# Revit family: PC6080B
name_source: partatom
category: Luminarias
units: mm (PartAtom-declared; Revit-internal decimal feet)

## family parameters
Compartido = Sí
Corte con vacíos al cargar = No
Cota de conector redondo = Diámetro de uso
Origen de luz = No
Punto de cálculo de habitación = No
Se basa en plano de trabajo = Sí
Siempre vertical = No
Tipo de pieza = Normal

## types (1)
- PERFIL_PC6080B
    Descripción = PERFIL DE ALUMINIO EN FORMA DE “H” CON DIFUSOR LECHOSO, PARA ALOJAR DOS TIRAS LUMINOSAS O TABLETAS, PERFIL DE COLOCACION SUPERIOR DE 19.2MM DE ANCHO E INFERIOR DE 31.4MM CON ESPACIO PARA DRIVER INTERIOR. INSTALACION SOBRE SUPERFICIES, CUENTA CON PIEZAS DE SUJECION PARA DIRIGIR LA CANALETA Y DESPLAZARLA, PERFIL PARA SUSPENDER. IDEAL PARA ATENUAR EL BRILLO E INCORPORAR LA LUZ AL AMBIENTE.PRESENTACION DESDE 0.5 - 3 METROS, REQUEIRE ACCESORIOS COMO TAPA FINAL (CONSIDERAR 1 PAR DE PZAS POR SEGMENTO DE PERFIL) Y TENSORES PARA SUSPENDER (CONSIDERAR 3PZAS POR SEGMENTO DE PERFIL).
    Elevación por defecto = 1219 mm
    Fabricante = BRILLANT
    Longitud = 1000 mm  [stored 3.28084 ft]
    Modelo = PC6080B
    Tapa Final 6080B.1 = 1
    Tensor 6080B.2 = 3

note: [stored X ft] marks values corroborated as IEEE doubles in the binary element streams (Revit-internal decimal feet)

## geometry (parser evidence)
native form markers: Blend x2
no freeform markers — native parametric forms only
